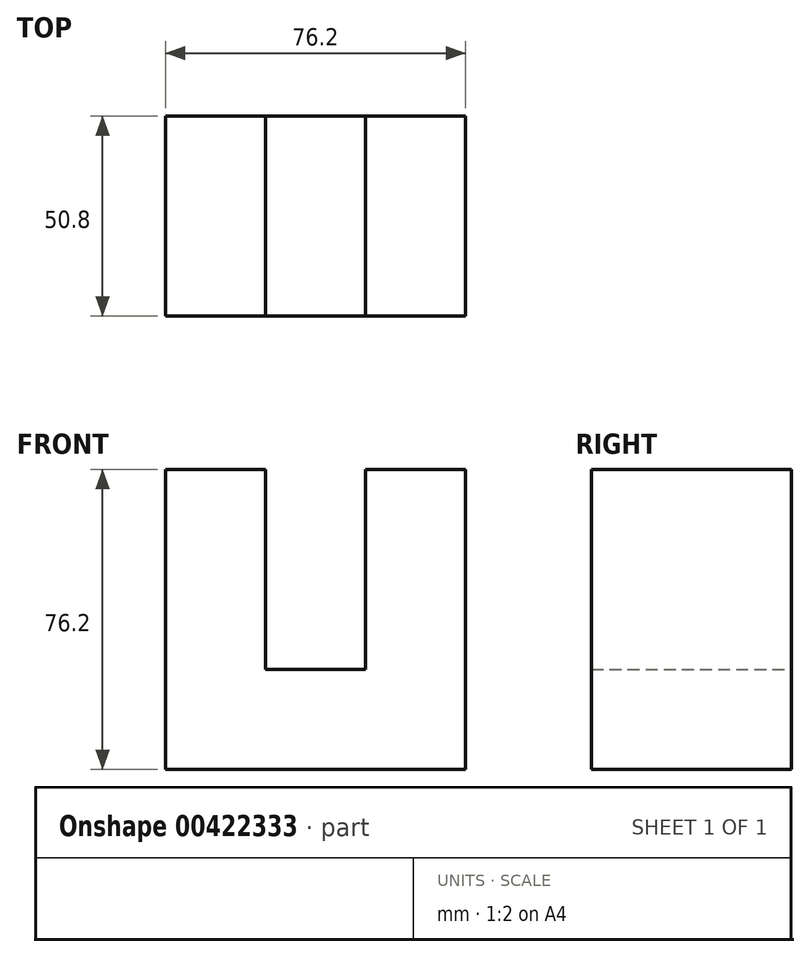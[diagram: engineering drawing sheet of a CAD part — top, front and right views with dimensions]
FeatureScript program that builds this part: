
annotation { "Feature Type Name" : "Feature", "Feature Type Description" : "" }
export const myFeature = defineFeature(function(context is Context, id is Id, definition is map)
    precondition{}
    {
        {
            var Q0;
            Q0=qCreatedBy(makeId("Front.planeOp"),FACE);
            var sketch = newSketch(context, id + "F0", { "sketchPlane" : qUnion([Q0])});
            skLineSegment(sketch, "E0", {"start": v(0, 0) * mm, "end": v(76.2, 0) * mm});
            skLineSegment(sketch, "E1", {"start": v(76.2, 0) * mm, "end": v(76.2, 76.2) * mm});
            skLineSegment(sketch, "E2", {"start": v(76.2, 76.2) * mm, "end": v(50.8, 76.2) * mm});
            skLineSegment(sketch, "E3", {"start": v(50.8, 76.2) * mm, "end": v(50.8, 25.4) * mm});
            skLineSegment(sketch, "E4", {"start": v(50.8, 25.4) * mm, "end": v(25.4, 25.4) * mm});
            skLineSegment(sketch, "E5", {"start": v(25.4, 25.4) * mm, "end": v(25.4, 76.2) * mm});
            skLineSegment(sketch, "E6", {"start": v(25.4, 76.2) * mm, "end": v(0, 76.2) * mm});
            skLineSegment(sketch, "E7", {"start": v(0, 76.2) * mm, "end": v(0, 0) * mm});
            skSolve(sketch);
        }
        {
            var Q0;
            Q0 = qSketchRegion(id + "F0", true);
            extrude(context, id + "F1", {"entities" : qUnion([Q0]), "depth" : 50.8 * mm});
        }
    });
